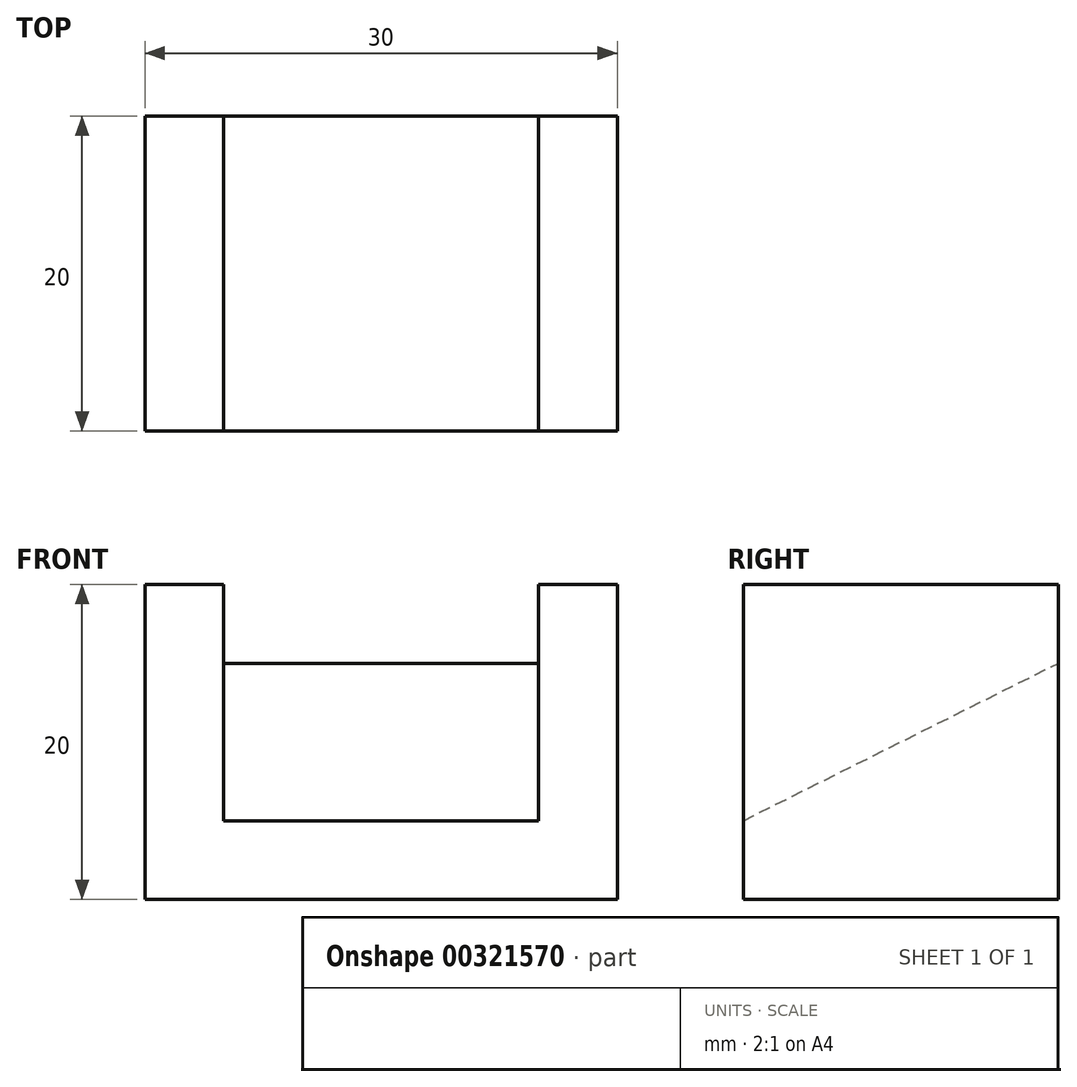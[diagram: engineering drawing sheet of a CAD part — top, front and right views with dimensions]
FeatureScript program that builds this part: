
annotation { "Feature Type Name" : "Feature", "Feature Type Description" : "" }
export const myFeature = defineFeature(function(context is Context, id is Id, definition is map)
    precondition{}
    {
        {
            var Q0;
            Q0=qCreatedBy(makeId("Right.planeOp"),FACE);
            var sketch = newSketch(context, id + "F0", { "sketchPlane" : qUnion([Q0])});
            skLineSegment(sketch, "E0.bottom", {"start": v(0, 0) * mm, "end": v(20, 0) * mm});
            skLineSegment(sketch, "E0.top", {"start": v(0, 20) * mm, "end": v(20, 20) * mm});
            skLineSegment(sketch, "E0.left", {"start": v(0, 0) * mm, "end": v(0, 20) * mm});
            skLineSegment(sketch, "E0.right", {"start": v(20, 0) * mm, "end": v(20, 20) * mm});
            skSolve(sketch);
        }
        {
            var Q0;
            Q0 = qSketchRegion(id + "F0", true);
            extrude(context, id + "F1", {"entities" : qUnion([Q0]), "depth" : 30 * mm});
        }
        {
            var Q0;
            Q0=makeQuery(id+"F1.opExtrude","CAP_FACE",FACE,{"disambiguationData":[OSD([sQuery(id+"F0.wireOp",EDGE,"E0.bottom"),sQuery(id+"F0.wireOp",EDGE,"E0.top"),sQuery(id+"F0.wireOp",EDGE,"E0.left"),sQuery(id+"F0.wireOp",EDGE,"E0.right")])],"isStart":false});
            var sketch = newSketch(context, id + "F2", { "sketchPlane" : qUnion([Q0])});
            skLineSegment(sketch, "E1", {"start": v(0, 5) * mm, "end": v(20, 15) * mm});
            skLineSegment(sketch, "E2", {"start": v(0, 20) * mm, "end": v(0, 5) * mm});
            skLineSegment(sketch, "E3", {"start": v(0, 20) * mm, "end": v(20, 20) * mm});
            skLineSegment(sketch, "E4", {"start": v(20, 20) * mm, "end": v(20, 15) * mm});
            skSolve(sketch);
        }
        {
            var Q0;
            Q0 = qSketchRegion(id + "F2", true);
            extrude(context, id + "F3", {"entities" : qUnion([Q0]), "operationType" : NewBodyOperationType.REMOVE, "oppositeDirection" : true, "depth" : 25 * mm, "hasSecondDirection" : true, "secondDirectionOppositeDirection" : true, "secondDirectionDepth" : 5 * mm});
        }
    });
